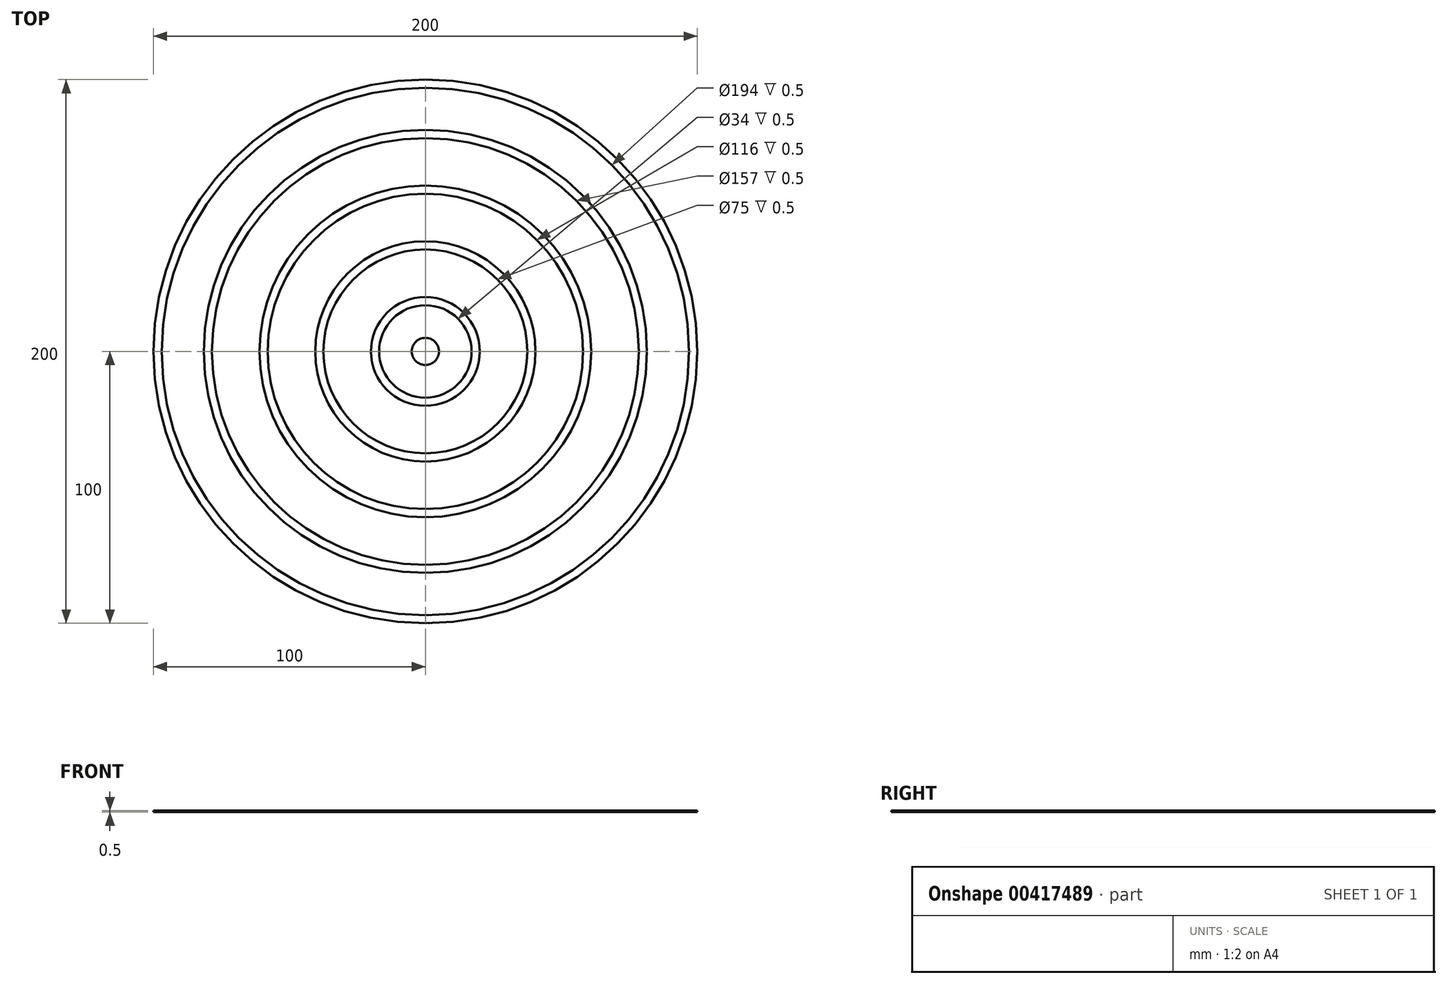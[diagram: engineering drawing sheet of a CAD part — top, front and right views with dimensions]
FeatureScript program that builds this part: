
annotation { "Feature Type Name" : "Feature", "Feature Type Description" : "" }
export const myFeature = defineFeature(function(context is Context, id is Id, definition is map)
    precondition{}
    {
        {
            var Q0;
            Q0=qCreatedBy(makeId("Top.planeOp"),FACE);
            var sketch = newSketch(context, id + "F0", { "sketchPlane" : qUnion([Q0])});
            skCircle(sketch, "E0", {"center": v(0, 0) * mm, "radius": 61 * mm});
            skCircle(sketch, "E1", {"center": v(0, 0) * mm, "radius": 20 * mm});
            skCircle(sketch, "E2", {"center": v(0, 0) * mm, "radius": 40.5 * mm});
            skCircle(sketch, "E3", {"center": v(0, 0) * mm, "radius": 100 * mm});
            skCircle(sketch, "E4", {"center": v(0, 0) * mm, "radius": 81.5 * mm});
            skCircle(sketch, "E5.0", {"center": v(0, 0) * mm, "radius": 97 * mm});
            skCircle(sketch, "E6.0", {"center": v(0, 0) * mm, "radius": 78.5 * mm});
            skCircle(sketch, "E7.0", {"center": v(0, 0) * mm, "radius": 58 * mm});
            skCircle(sketch, "E8.0", {"center": v(0, 0) * mm, "radius": 37.5 * mm});
            skCircle(sketch, "E9.0", {"center": v(0, 0) * mm, "radius": 17 * mm});
            skCircle(sketch, "E10", {"center": v(0, 0) * mm, "radius": 5 * mm});
            skSolve(sketch);
        }
        {
            var Q0;
            Q0=makeQuery(id+"F0.imprint","IMPRINT",FACE,{"disambiguationData":[TD([[makeQuery(id+"F0.imprint","IMPRINT",EDGE,{"derivedFrom":sQuery(id+"F0.wireOp",EDGE,"E3")}),1.0]])]});
            var Q1;
            Q1=makeQuery(id+"F0.imprint","IMPRINT",FACE,{"disambiguationData":[TD([[makeQuery(id+"F0.imprint","IMPRINT",EDGE,{"derivedFrom":sQuery(id+"F0.wireOp",EDGE,"E4")}),1.0]])]});
            var Q2;
            Q2=makeQuery(id+"F0.imprint","IMPRINT",FACE,{"disambiguationData":[TD([[makeQuery(id+"F0.imprint","IMPRINT",EDGE,{"derivedFrom":sQuery(id+"F0.wireOp",EDGE,"E0")}),1.0]])]});
            var Q3;
            Q3=makeQuery(id+"F0.imprint","IMPRINT",FACE,{"disambiguationData":[TD([[makeQuery(id+"F0.imprint","IMPRINT",EDGE,{"derivedFrom":sQuery(id+"F0.wireOp",EDGE,"E2")}),1.0]])]});
            var Q4;
            Q4=makeQuery(id+"F0.imprint","IMPRINT",FACE,{"disambiguationData":[TD([[makeQuery(id+"F0.imprint","IMPRINT",EDGE,{"derivedFrom":sQuery(id+"F0.wireOp",EDGE,"E1")}),1.0]])]});
            var Q5;
            Q5=makeQuery(id+"F0.imprint","IMPRINT",FACE,{"disambiguationData":[TD([[makeQuery(id+"F0.imprint","IMPRINT",EDGE,{"derivedFrom":sQuery(id+"F0.wireOp",EDGE,"E10")}),1.0]])]});
            extrude(context, id + "F1", {"entities" : qUnion([Q0, Q1, Q2, Q3, Q4, Q5]), "depth" : .5 * mm});
        }
    });
